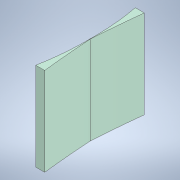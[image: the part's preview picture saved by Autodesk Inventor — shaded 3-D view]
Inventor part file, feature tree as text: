
AUTODESK INVENTOR PART (.ipt)
format: ipt  version: 2021 (Build 250183000, 183)  size: 138,752 bytes
history: native  units: mm
features: extrude x1, sketch x1
ambient origin geometry x8: Origin, YZ Plane, XZ Plane, XY Plane, X Axis, Y Axis, Z Axis, Center Point
bodies: Solid1 (feature_tree)
feature tree (2):
  extrude  "Extrusion1"  Depth=150.0mm
  sketch  "Sketch1"  dims[d0=85.0mm d1=14.835299mm d2=430.0mm d3=85.0mm d4=14.835299mm d5=430.0mm d6=85.0mm d7=16.580628mm d10=85.0mm d11=16.580628mm d12=150.0mm d13=0.0mm]
